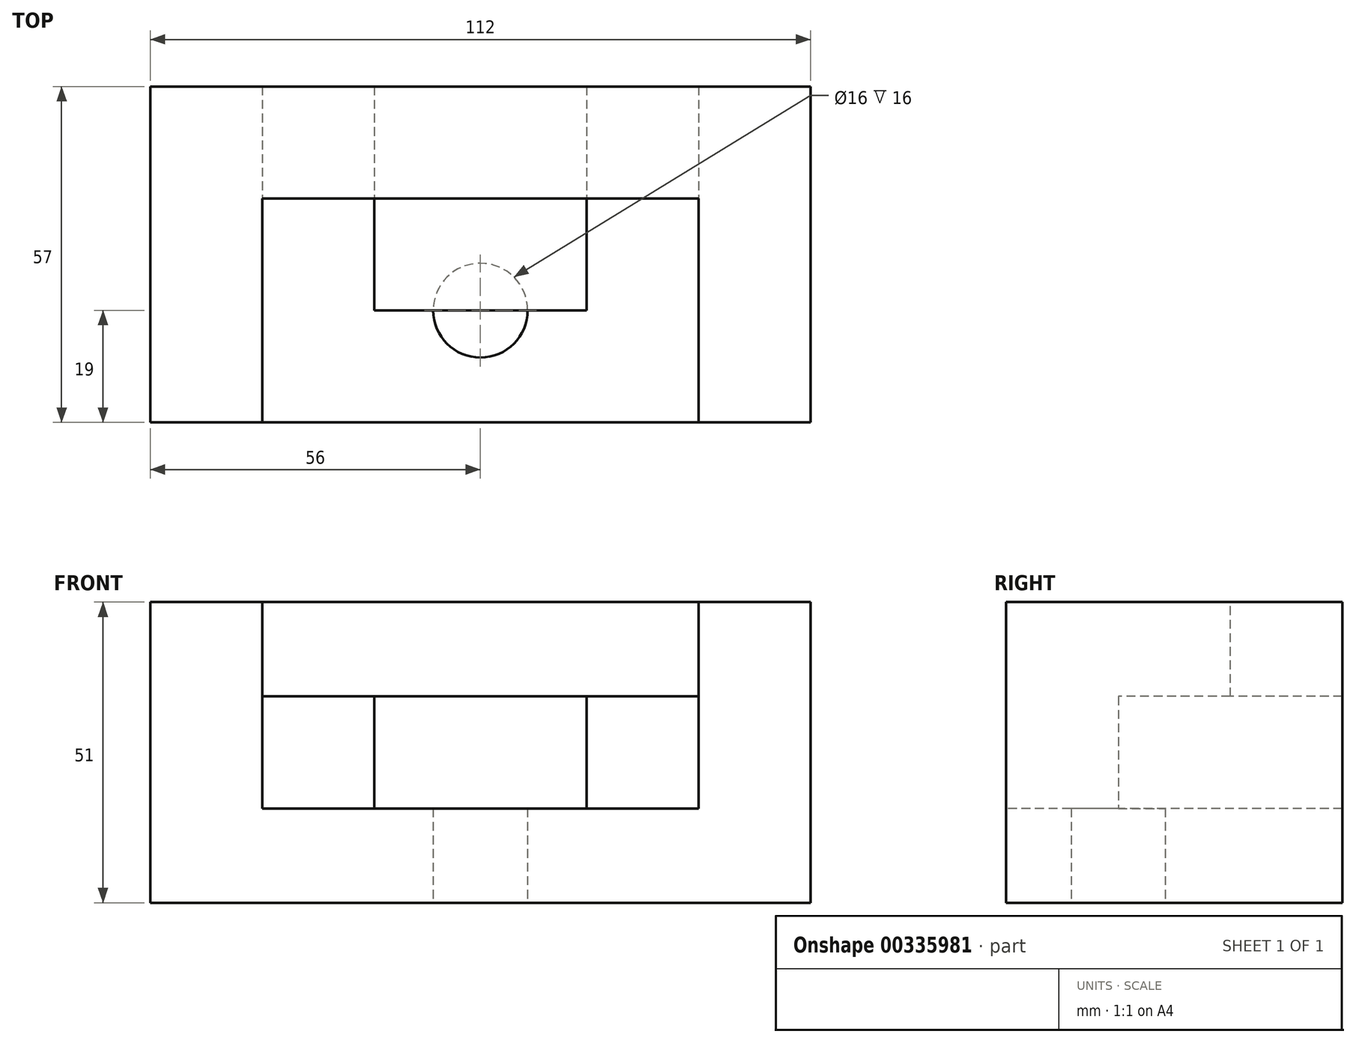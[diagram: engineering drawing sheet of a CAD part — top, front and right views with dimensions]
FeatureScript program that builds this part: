
annotation { "Feature Type Name" : "Feature", "Feature Type Description" : "" }
export const myFeature = defineFeature(function(context is Context, id is Id, definition is map)
    precondition{}
    {
        {
            var Q0;
            Q0=qCreatedBy(makeId("Front.planeOp"),FACE);
            var sketch = newSketch(context, id + "F0", { "sketchPlane" : qUnion([Q0])});
            skLineSegment(sketch, "E0.bottom", {"start": v(0, 0) * mm, "end": v(112, 0) * mm});
            skLineSegment(sketch, "E0.top", {"start": v(0, 51) * mm, "end": v(112, 51) * mm});
            skLineSegment(sketch, "E0.left", {"start": v(0, 0) * mm, "end": v(0, 51) * mm});
            skLineSegment(sketch, "E0.right", {"start": v(112, 0) * mm, "end": v(112, 51) * mm});
            skSolve(sketch);
        }
        {
            var Q0;
            Q0 = qSketchRegion(id + "F0", true);
            extrude(context, id + "F1", {"entities" : qUnion([Q0]), "oppositeDirection" : true, "depth" : 57 * mm});
        }
        {
            var Q0;
            Q0=makeQuery(id+"F1.opExtrude","CAP_FACE",FACE,{"disambiguationData":[OSD([sQuery(id+"F0.wireOp",EDGE,"E0.bottom"),sQuery(id+"F0.wireOp",EDGE,"E0.top"),sQuery(id+"F0.wireOp",EDGE,"E0.left"),sQuery(id+"F0.wireOp",EDGE,"E0.right")])],"isStart":true});
            var sketch = newSketch(context, id + "F2", { "sketchPlane" : qUnion([Q0])});
            skLineSegment(sketch, "E1", {"start": v(19, 51) * mm, "end": v(19, 16) * mm});
            skLineSegment(sketch, "E2", {"start": v(19, 16) * mm, "end": v(93, 16) * mm});
            skLineSegment(sketch, "E3", {"start": v(93, 16) * mm, "end": v(93, 51) * mm});
            skLineSegment(sketch, "E4", {"start": v(19, 35) * mm, "end": v(93, 35) * mm});
            skLineSegment(sketch, "E5", {"start": v(38, 35) * mm, "end": v(38, 16) * mm});
            skLineSegment(sketch, "E6", {"start": v(74, 35) * mm, "end": v(74, 16) * mm});
            skSolve(sketch);
        }
        {
            var Q0;
            {var subQ3=sQuery(id+"F2.wireOp",EDGE,"E1");var subQ6=makeQuery(id+"F1.opExtrude","CAP_EDGE",EDGE,{"disambiguationData":[OSD([sQuery(id+"F0.wireOp",EDGE,"E0.top")])],"isStart":true});var subQ9=makeQuery(id+"F2.imprint","INTERSECT",VERTEX,{"derivedFrom":[subQ6,subQ3]});Q0=makeQuery(id+"F2.imprint","IMPRINT",FACE,{"disambiguationData":[TD([[makeQuery(id+"F2.imprint","IMPRINT",EDGE,{"disambiguationData":[TD([[subQ9,-1.0]])],"derivedFrom":subQ3}),1.0]])]});}
            extrude(context, id + "F3", {"entities" : qUnion([Q0]), "operationType" : NewBodyOperationType.REMOVE, "oppositeDirection" : true, "depth" : 38 * mm});
        }
        {
            var Q0;
            {var subQ3=sQuery(id+"F2.wireOp",EDGE,"E6");Q0=makeQuery(id+"F2.imprint","IMPRINT",FACE,{"disambiguationData":[TD([[makeQuery(id+"F2.imprint","IMPRINT",EDGE,{"derivedFrom":subQ3}),1.0]])]});}
            var Q1;
            {var subQ5=sQuery(id+"F2.wireOp",EDGE,"E5");Q1=makeQuery(id+"F2.imprint","IMPRINT",FACE,{"disambiguationData":[TD([[makeQuery(id+"F2.imprint","IMPRINT",EDGE,{"derivedFrom":subQ5}),-1.0]])]});}
            extrude(context, id + "F4", {"entities" : qUnion([Q0, Q1]), "operationType" : NewBodyOperationType.REMOVE, "endBound" : BoundingType.THROUGH_ALL, "oppositeDirection" : true, "depth" : 25 * mm});
        }
        {
            var Q0;
            {var subQ0=sQuery(id+"F2.wireOp",EDGE,"E5");Q0=makeQuery(id+"F2.imprint","IMPRINT",FACE,{"disambiguationData":[TD([[makeQuery(id+"F2.imprint","IMPRINT",EDGE,{"derivedFrom":subQ0}),1.0]])]});}
            extrude(context, id + "F5", {"entities" : qUnion([Q0]), "operationType" : NewBodyOperationType.REMOVE, "oppositeDirection" : true, "depth" : 19 * mm});
        }
        {
            var Q0;
            Q0=makeQuery(id+"F1.opExtrude","SWEPT_FACE",FACE,{"disambiguationData":[OSD([sQuery(id+"F0.wireOp",EDGE,"E0.bottom")])]});
            var sketch = newSketch(context, id + "F6", { "sketchPlane" : qUnion([Q0])});
            skCircle(sketch, "E7", {"center": v(56, -19) * mm, "radius": 8 * mm});
            skSolve(sketch);
        }
        {
            var Q0;
            Q0 = qSketchRegion(id + "F6", true);
            extrude(context, id + "F7", {"entities" : qUnion([Q0]), "operationType" : NewBodyOperationType.REMOVE, "oppositeDirection" : true, "depth" : 16 * mm});
        }
    });
